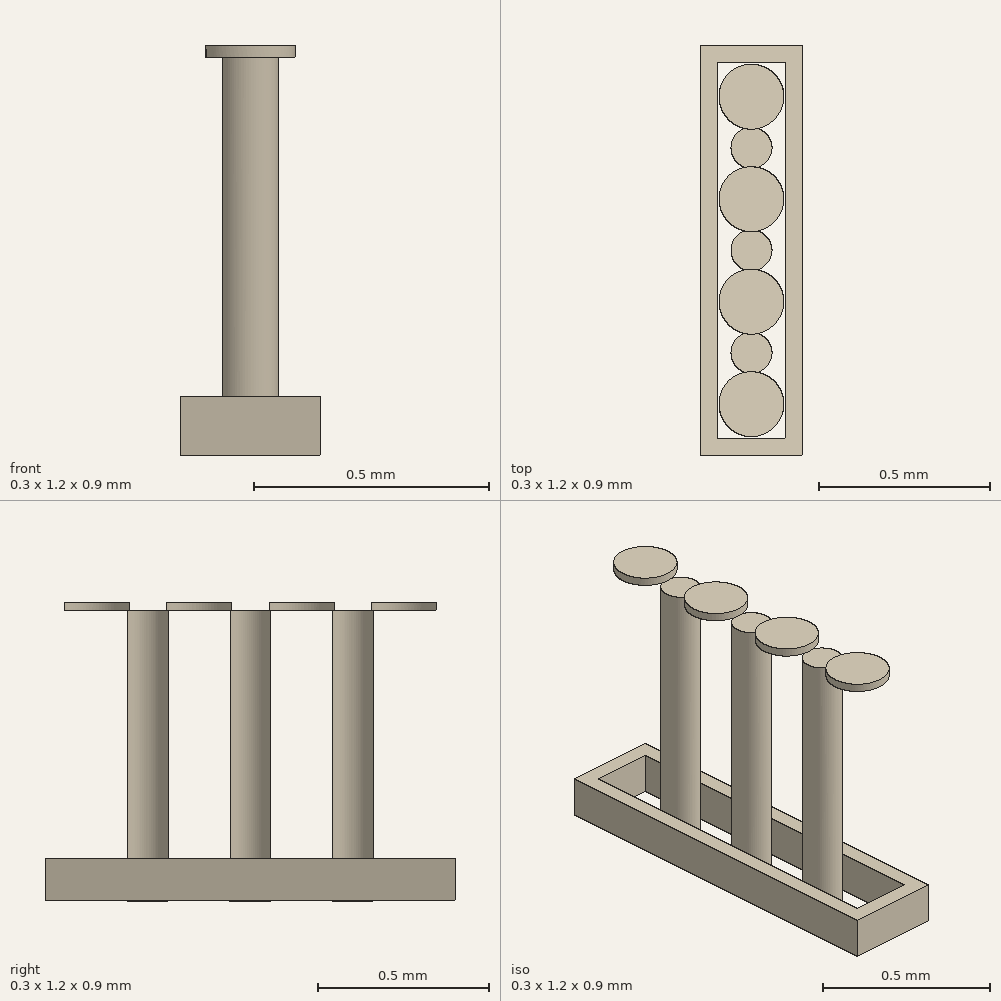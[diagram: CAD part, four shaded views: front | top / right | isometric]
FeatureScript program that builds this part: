
annotation { "Feature Type Name" : "Feature", "Feature Type Description" : "" }
export const myFeature = defineFeature(function(context is Context, id is Id, definition is map)
    precondition{}
    {
        {
            var Q0;
            Q0=qCreatedBy(makeId("Front.planeOp"),FACE);
            var sketch = newSketch(context, id + "F0", { "sketchPlane" : qUnion([Q0])});
            skLineSegment(sketch, "E0.bottom", {"start": v(-6.16, 0.55) * mm, "end": v(-5.86, 0.55) * mm});
            skLineSegment(sketch, "E0.top", {"start": v(-6.16, 0.42) * mm, "end": v(-5.86, 0.42) * mm});
            skLineSegment(sketch, "E0.left", {"start": v(-6.16, 0.55) * mm, "end": v(-6.16, 0.42) * mm});
            skLineSegment(sketch, "E0.right", {"start": v(-5.86, 0.55) * mm, "end": v(-5.86, 0.42) * mm});
            skSolve(sketch);
        }
        {
            var Q0;
            Q0 = qSketchRegion(id + "F0", true);
            extrude(context, id + "F1", {"entities" : qUnion([Q0]), "oppositeDirection" : true, "depth" : 1.2 * mm});
        }
        {
            var Q0;
            Q0=makeQuery(id+"F1.opExtrude","SWEPT_FACE",FACE,{"disambiguationData":[OSD([sQuery(id+"F0.wireOp",EDGE,"E0.bottom")])]});
            var sketch = newSketch(context, id + "F2", { "sketchPlane" : qUnion([Q0])});
            skCircle(sketch, "E1", {"center": v(-6, 0.15) * mm, "radius": 0.1 * mm});
            skCircle(sketch, "E2", {"center": v(-6, 0.45) * mm, "radius": 0.1 * mm});
            skCircle(sketch, "E3", {"center": v(-6, 0.75) * mm, "radius": 0.1 * mm});
            skCircle(sketch, "E4", {"center": v(-6, 1.05) * mm, "radius": 0.1 * mm});
            skSolve(sketch);
        }
        {
            var Q0;
            Q0 = qSketchRegion(id + "F2", true);
            extrude(context, id + "F3", {"entities" : qUnion([Q0]), "operationType" : NewBodyOperationType.ADD, "depth" : .75 * mm});
        }
        {
            var Q0;
            Q0=makeQuery(id+"F1.opExtrude","SWEPT_FACE",FACE,{"disambiguationData":[OSD([sQuery(id+"F0.wireOp",EDGE,"E0.top")])]});
            var sketch = newSketch(context, id + "F4", { "sketchPlane" : qUnion([Q0])});
            skCircle(sketch, "E5", {"center": v(-6, -0.15) * mm, "radius": 0.05 * mm});
            skPoint(sketch, "E5.centerSnap0", {"position": v(-6, 0) * mm});
            skCircle(sketch, "E6", {"center": v(-6, -0.3) * mm, "radius": 0.06 * mm});
            skCircle(sketch, "E7", {"center": v(-6, -0.45) * mm, "radius": 0.05 * mm});
            skCircle(sketch, "E8", {"center": v(-6, -0.6) * mm, "radius": 0.06 * mm});
            skCircle(sketch, "E9", {"center": v(-6, -0.75) * mm, "radius": 0.05 * mm});
            skCircle(sketch, "E10", {"center": v(-6, -0.9) * mm, "radius": 0.06 * mm});
            skCircle(sketch, "E11", {"center": v(-6, -1.05) * mm, "radius": 0.05 * mm});
            skSolve(sketch);
        }
        {
            var Q0;
            Q0=makeQuery(id+"F4.imprint","IMPRINT",FACE,{"disambiguationData":[TD([[makeQuery(id+"F4.imprint","IMPRINT",EDGE,{"derivedFrom":sQuery(id+"F4.wireOp",EDGE,"E5")}),-1.0]])]});
            var sketch = newSketch(context, id + "F5", { "sketchPlane" : qUnion([Q0])});
            skLineSegment(sketch, "E12.bottom", {"start": v(-5.9, -0.05) * mm, "end": v(-6.1, -0.05) * mm});
            skLineSegment(sketch, "E12.top", {"start": v(-5.9, -1.15) * mm, "end": v(-6.1, -1.15) * mm});
            skLineSegment(sketch, "E12.left", {"start": v(-5.9, -0.05) * mm, "end": v(-5.9, -1.15) * mm});
            skLineSegment(sketch, "E12.right", {"start": v(-6.1, -0.05) * mm, "end": v(-6.1, -1.15) * mm});
            skSolve(sketch);
        }
        {
            var Q0;
            Q0 = qSketchRegion(id + "F5", true);
            extrude(context, id + "F6", {"entities" : qUnion([Q0]), "operationType" : NewBodyOperationType.REMOVE, "oppositeDirection" : true, "depth" : .85 * mm});
        }
        {
            var Q0;
            Q0=makeQuery(id+"F4.imprint","IMPRINT",FACE,{"disambiguationData":[TD([[makeQuery(id+"F4.imprint","IMPRINT",EDGE,{"derivedFrom":sQuery(id+"F4.wireOp",EDGE,"E11")}),1.0]])]});
            var Q1;
            Q1=makeQuery(id+"F4.imprint","IMPRINT",FACE,{"disambiguationData":[TD([[makeQuery(id+"F4.imprint","IMPRINT",EDGE,{"derivedFrom":sQuery(id+"F4.wireOp",EDGE,"E9")}),1.0]])]});
            var Q2;
            Q2=makeQuery(id+"F4.imprint","IMPRINT",FACE,{"disambiguationData":[TD([[makeQuery(id+"F4.imprint","IMPRINT",EDGE,{"derivedFrom":sQuery(id+"F4.wireOp",EDGE,"E7")}),1.0]])]});
            var Q3;
            Q3=makeQuery(id+"F4.imprint","IMPRINT",FACE,{"disambiguationData":[TD([[makeQuery(id+"F4.imprint","IMPRINT",EDGE,{"derivedFrom":sQuery(id+"F4.wireOp",EDGE,"E5")}),1.0]])]});
            var Q4;
            Q4=sQuery(id+"F4.wireOp",EDGE,"E11");
            var Q5;
            Q5=sQuery(id+"F4.wireOp",EDGE,"E9");
            var Q6;
            Q6=sQuery(id+"F4.wireOp",EDGE,"E7");
            var Q7;
            Q7=sQuery(id+"F4.wireOp",EDGE,"E5");
            extrude(context, id + "F7", {"entities" : qUnion([Q0, Q1, Q2, Q3]), "operationType" : NewBodyOperationType.REMOVE, "surfaceEntities" : qUnion([Q4, Q5, Q6, Q7]), "oppositeDirection" : true, "depth" : .185 * mm});
        }
        {
            var Q0;
            Q0=makeQuery(id+"F4.imprint","IMPRINT",FACE,{"disambiguationData":[TD([[makeQuery(id+"F4.imprint","IMPRINT",EDGE,{"derivedFrom":sQuery(id+"F4.wireOp",EDGE,"E10")}),1.0]])]});
            var Q1;
            Q1=makeQuery(id+"F4.imprint","IMPRINT",FACE,{"disambiguationData":[TD([[makeQuery(id+"F4.imprint","IMPRINT",EDGE,{"derivedFrom":sQuery(id+"F4.wireOp",EDGE,"E8")}),1.0]])]});
            var Q2;
            Q2=makeQuery(id+"F4.imprint","IMPRINT",FACE,{"disambiguationData":[TD([[makeQuery(id+"F4.imprint","IMPRINT",EDGE,{"derivedFrom":sQuery(id+"F4.wireOp",EDGE,"E6")}),1.0]])]});
            extrude(context, id + "F8", {"entities" : qUnion([Q0, Q1, Q2]), "operationType" : NewBodyOperationType.ADD, "oppositeDirection" : true, "depth" : .85 * mm});
        }
    });
